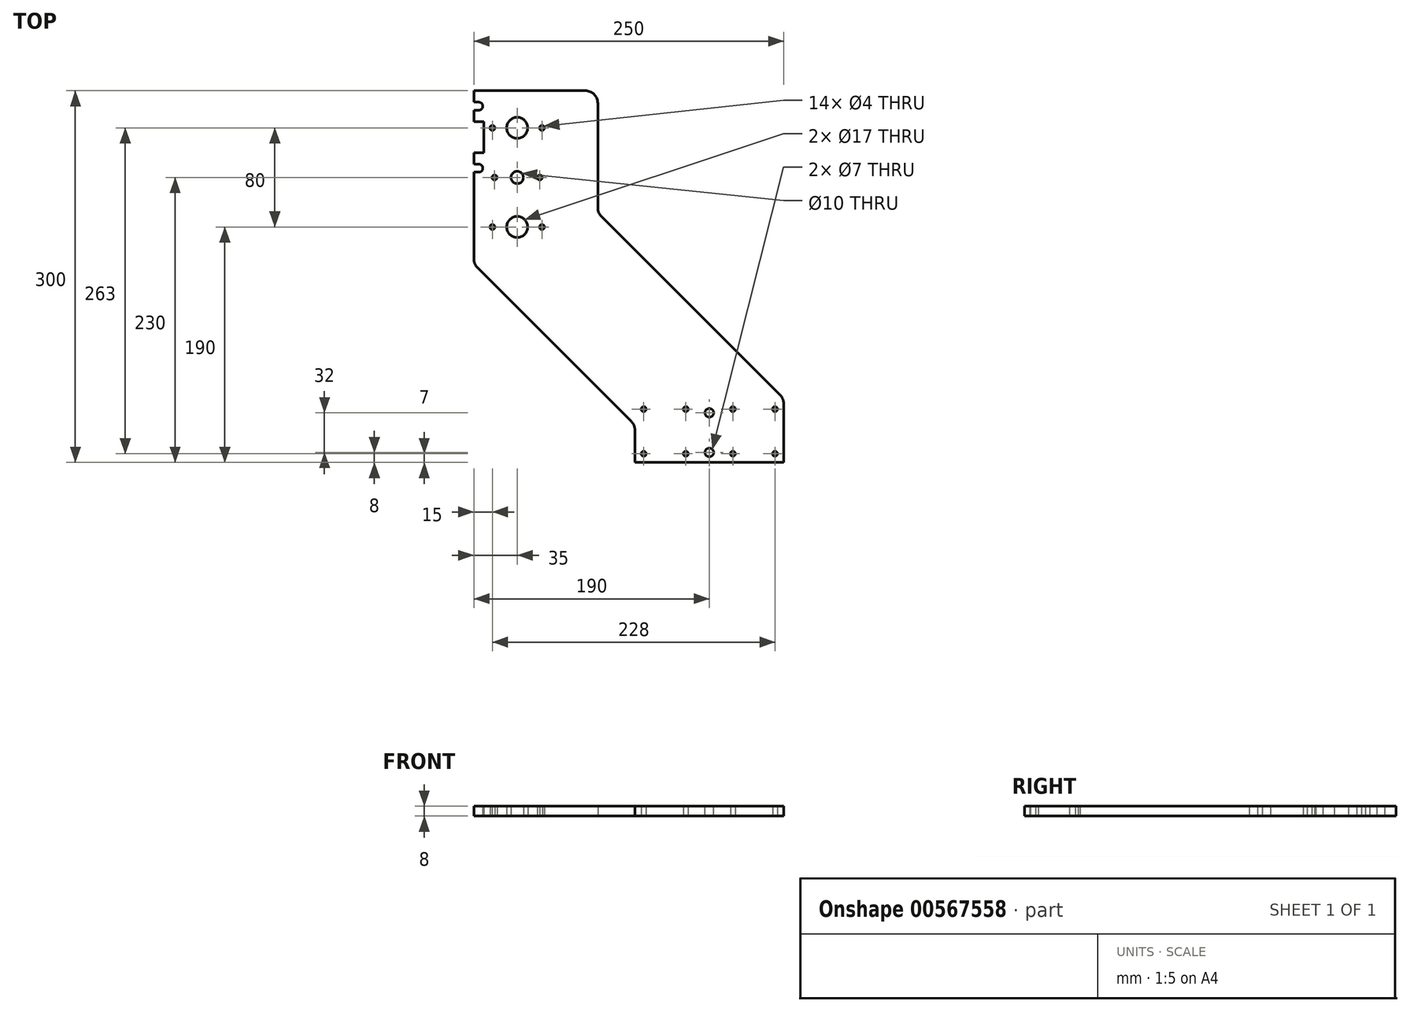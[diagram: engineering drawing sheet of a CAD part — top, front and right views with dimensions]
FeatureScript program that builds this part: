
annotation { "Feature Type Name" : "Feature", "Feature Type Description" : "" }
export const myFeature = defineFeature(function(context is Context, id is Id, definition is map)
    precondition{}
    {
        {
            var Q0;
            Q0=qCreatedBy(makeId("Top.planeOp"),FACE);
            var sketch = newSketch(context, id + "F0", { "sketchPlane" : qUnion([Q0])});
            skLineSegment(sketch, "E0", {"start": v(0, 0) * mm, "end": v(120, 0) * mm});
            skLineSegment(sketch, "E1", {"start": v(120, 0) * mm, "end": v(120, 51.42) * mm});
            skLineSegment(sketch, "E2", {"start": v(120, 51.42) * mm, "end": v(-30, 201.42) * mm});
            skLineSegment(sketch, "E3", {"start": v(-30, 201.42) * mm, "end": v(-30, 300) * mm});
            skLineSegment(sketch, "E4", {"start": v(-30, 300) * mm, "end": v(-130, 300) * mm});
            skLineSegment(sketch, "E5", {"start": v(-130, 300) * mm, "end": v(-130, 290.75) * mm});
            skLineSegment(sketch, "E6", {"start": v(-130, 160) * mm, "end": v(0, 30) * mm});
            skLineSegment(sketch, "E7", {"start": v(0, 30) * mm, "end": v(0, 0) * mm});
            skCircle(sketch, "E8", {"center": v(7, 43) * mm, "radius": 2 * mm});
            skCircle(sketch, "E9", {"center": v(7, 7) * mm, "radius": 2 * mm});
            skCircle(sketch, "E10", {"center": v(41, 43) * mm, "radius": 2 * mm});
            skCircle(sketch, "E11", {"center": v(41, 7) * mm, "radius": 2 * mm});
            skLineSegment(sketch, "E12", {"start": v(60, 0) * mm, "end": v(60, 107.18) * mm, "construction": true});
            skCircle(sketch, "E13.MirrorC", {"center": v(79, 43) * mm, "radius": 2 * mm});
            skCircle(sketch, "E14.MirrorC", {"center": v(113, 43) * mm, "radius": 2 * mm});
            skCircle(sketch, "E15.MirrorC", {"center": v(113, 7) * mm, "radius": 2 * mm});
            skCircle(sketch, "E16.MirrorC", {"center": v(79, 7) * mm, "radius": 2 * mm});
            skCircle(sketch, "E17", {"center": v(-95, 270) * mm, "radius": 8.5 * mm});
            skCircle(sketch, "E18", {"center": v(-95, 190) * mm, "radius": 8.5 * mm});
            skPoint(sketch, "E19", {"position": v(-80, 300) * mm});
            skCircle(sketch, "E20", {"center": v(-75, 270) * mm, "radius": 2 * mm});
            skCircle(sketch, "E21", {"center": v(-115, 270) * mm, "radius": 2 * mm});
            skCircle(sketch, "E22", {"center": v(-75, 190) * mm, "radius": 2 * mm});
            skCircle(sketch, "E23", {"center": v(-115, 190) * mm, "radius": 2 * mm});
            skLineSegment(sketch, "E24", {"start": v(-115, 190) * mm, "end": v(-75, 190) * mm, "construction": true});
            skLineSegment(sketch, "E25", {"start": v(-75, 270) * mm, "end": v(-115, 270) * mm, "construction": true});
            skLineSegment(sketch, "E26.bottom", {"start": v(-130, 275) * mm, "end": v(-122, 275) * mm});
            skLineSegment(sketch, "E26.top", {"start": v(-130, 250) * mm, "end": v(-122, 250) * mm});
            skLineSegment(sketch, "E26.right", {"start": v(-122, 275) * mm, "end": v(-122, 250) * mm});
            skLineSegment(sketch, "E27.trimOffspring", {"start": v(-130, 250) * mm, "end": v(-130, 160) * mm});
            skArc(sketch, "E28", {"start": v(-126, 284.25) * mm, "mid": v(-122.75, 287.5) * mm, "end": v(-126, 290.75) * mm});
            skLineSegment(sketch, "E29", {"start": v(-126, 290.75) * mm, "end": v(-130, 290.75) * mm});
            skLineSegment(sketch, "E30", {"start": v(-126, 284.25) * mm, "end": v(-130, 284.25) * mm});
            skLineSegment(sketch, "E31.trimOffspring", {"start": v(-130, 284.25) * mm, "end": v(-130, 275) * mm});
            skLineSegment(sketch, "E32", {"start": v(-89.75, 262.5) * mm, "end": v(-122, 262.5) * mm, "construction": true});
            skLineSegment(sketch, "E33.MirrorCS", {"start": v(-126, 240.75) * mm, "end": v(-130, 240.75) * mm});
            skArc(sketch, "E34.MirrorCS", {"start": v(-126, 240.75) * mm, "mid": v(-122.75, 237.5) * mm, "end": v(-126, 234.25) * mm});
            skLineSegment(sketch, "E35.MirrorCS", {"start": v(-126, 234.25) * mm, "end": v(-130, 234.25) * mm});
            skSolve(sketch);
        }
        {
            var Q0;
            Q0=makeQuery(id+"F0.imprint","IMPRINT",FACE,{"disambiguationData":[TD([[makeQuery(id+"F0.imprint","IMPRINT",EDGE,{"derivedFrom":sQuery(id+"F0.wireOp",EDGE,"E0")}),1.0]])]});
            extrude(context, id + "F1", {"entities" : qUnion([Q0]), "depth" : 8 * mm, "offsetDistance" : 25 * mm});
        }
        {
            var Q0;
            Q0=makeQuery(id+"F1.opExtrude","CAP_FACE",FACE,{"disambiguationData":[OSD([sQuery(id+"F0.wireOp",EDGE,"E0"),sQuery(id+"F0.wireOp",EDGE,"E1"),sQuery(id+"F0.wireOp",EDGE,"E2"),sQuery(id+"F0.wireOp",EDGE,"E3"),sQuery(id+"F0.wireOp",EDGE,"E4"),sQuery(id+"F0.wireOp",EDGE,"E5"),sQuery(id+"F0.wireOp",EDGE,"E6"),sQuery(id+"F0.wireOp",EDGE,"E7"),sQuery(id+"F0.wireOp",EDGE,"E8"),sQuery(id+"F0.wireOp",EDGE,"E9"),sQuery(id+"F0.wireOp",EDGE,"E10"),sQuery(id+"F0.wireOp",EDGE,"E11"),sQuery(id+"F0.wireOp",EDGE,"E13.MirrorC"),sQuery(id+"F0.wireOp",EDGE,"E14.MirrorC"),sQuery(id+"F0.wireOp",EDGE,"E15.MirrorC"),sQuery(id+"F0.wireOp",EDGE,"E16.MirrorC"),sQuery(id+"F0.wireOp",EDGE,"E17"),sQuery(id+"F0.wireOp",EDGE,"E18"),sQuery(id+"F0.wireOp",EDGE,"E20"),sQuery(id+"F0.wireOp",EDGE,"E21"),sQuery(id+"F0.wireOp",EDGE,"E22"),sQuery(id+"F0.wireOp",EDGE,"E23"),sQuery(id+"F0.wireOp",EDGE,"E26.bottom"),sQuery(id+"F0.wireOp",EDGE,"E26.top"),sQuery(id+"F0.wireOp",EDGE,"E26.right"),sQuery(id+"F0.wireOp",EDGE,"E27.trimOffspring"),sQuery(id+"F0.wireOp",EDGE,"E28"),sQuery(id+"F0.wireOp",EDGE,"E29"),sQuery(id+"F0.wireOp",EDGE,"E30"),sQuery(id+"F0.wireOp",EDGE,"E31.trimOffspring"),sQuery(id+"F0.wireOp",EDGE,"E33.MirrorCS"),sQuery(id+"F0.wireOp",EDGE,"E34.MirrorCS"),sQuery(id+"F0.wireOp",EDGE,"E35.MirrorCS")])],"isStart":false});
            var sketch = newSketch(context, id + "F2", { "sketchPlane" : qUnion([Q0])});
            skCircle(sketch, "E36", {"center": v(60, 8) * mm, "radius": 3.5 * mm});
            skCircle(sketch, "E37", {"center": v(60, 40) * mm, "radius": 3.5 * mm});
            skSolve(sketch);
        }
        {
            var Q0;
            Q0 = qSketchRegion(id + "F2", true);
            extrude(context, id + "F3", {"entities" : qUnion([Q0]), "operationType" : NewBodyOperationType.REMOVE, "endBound" : BoundingType.UP_TO_NEXT, "oppositeDirection" : true, "depth" : 25 * mm, "offsetDistance" : 25 * mm});
        }
        {
            var Q0;
            Q0=makeQuery(id+"F1.opExtrude","CAP_FACE",FACE,{"disambiguationData":[OSD([sQuery(id+"F0.wireOp",EDGE,"E0"),sQuery(id+"F0.wireOp",EDGE,"E1"),sQuery(id+"F0.wireOp",EDGE,"E2"),sQuery(id+"F0.wireOp",EDGE,"E3"),sQuery(id+"F0.wireOp",EDGE,"E4"),sQuery(id+"F0.wireOp",EDGE,"E5"),sQuery(id+"F0.wireOp",EDGE,"E6"),sQuery(id+"F0.wireOp",EDGE,"E7"),sQuery(id+"F0.wireOp",EDGE,"E8"),sQuery(id+"F0.wireOp",EDGE,"E9"),sQuery(id+"F0.wireOp",EDGE,"E10"),sQuery(id+"F0.wireOp",EDGE,"E11"),sQuery(id+"F0.wireOp",EDGE,"E13.MirrorC"),sQuery(id+"F0.wireOp",EDGE,"E14.MirrorC"),sQuery(id+"F0.wireOp",EDGE,"E15.MirrorC"),sQuery(id+"F0.wireOp",EDGE,"E16.MirrorC"),sQuery(id+"F0.wireOp",EDGE,"E17"),sQuery(id+"F0.wireOp",EDGE,"E18"),sQuery(id+"F0.wireOp",EDGE,"E20"),sQuery(id+"F0.wireOp",EDGE,"E21"),sQuery(id+"F0.wireOp",EDGE,"E22"),sQuery(id+"F0.wireOp",EDGE,"E23"),sQuery(id+"F0.wireOp",EDGE,"E26.bottom"),sQuery(id+"F0.wireOp",EDGE,"E26.top"),sQuery(id+"F0.wireOp",EDGE,"E26.right"),sQuery(id+"F0.wireOp",EDGE,"E27.trimOffspring"),sQuery(id+"F0.wireOp",EDGE,"E28"),sQuery(id+"F0.wireOp",EDGE,"E29"),sQuery(id+"F0.wireOp",EDGE,"E30"),sQuery(id+"F0.wireOp",EDGE,"E31.trimOffspring"),sQuery(id+"F0.wireOp",EDGE,"E33.MirrorCS"),sQuery(id+"F0.wireOp",EDGE,"E34.MirrorCS"),sQuery(id+"F0.wireOp",EDGE,"E35.MirrorCS")])],"isStart":true});
            var sketch = newSketch(context, id + "F4", { "sketchPlane" : qUnion([Q0])});
            skLineSegment(sketch, "E38", {"start": v(-95, -270) * mm, "end": v(-95, -190) * mm, "construction": true});
            skCircle(sketch, "E39", {"center": v(-95, -230) * mm, "radius": 5 * mm});
            skLineSegment(sketch, "E40", {"start": v(-76.75, -230) * mm, "end": v(-113.25, -230) * mm, "construction": true});
            skCircle(sketch, "E41", {"center": v(-76.75, -230) * mm, "radius": 2 * mm});
            skCircle(sketch, "E42", {"center": v(-113.25, -230) * mm, "radius": 2 * mm});
            skSolve(sketch);
        }
        {
            var Q0;
            Q0 = qSketchRegion(id + "F4", true);
            extrude(context, id + "F5", {"entities" : qUnion([Q0]), "operationType" : NewBodyOperationType.REMOVE, "endBound" : BoundingType.UP_TO_NEXT, "oppositeDirection" : true, "depth" : 25 * mm, "offsetDistance" : 25 * mm});
        }
        {
            var Q0;
            Q0=makeQuery(id+"F1.opExtrude","SWEPT_EDGE",EDGE,{"disambiguationData":[OSD([sQuery(id+"F0.wireOp",EDGE,"E6"),sQuery(id+"F0.wireOp",EDGE,"E27.trimOffspring")])]});
            var Q1;
            Q1=makeQuery(id+"F1.opExtrude","SWEPT_EDGE",EDGE,{"disambiguationData":[OSD([sQuery(id+"F0.wireOp",EDGE,"E3"),sQuery(id+"F0.wireOp",EDGE,"E4")])]});
            var Q2;
            Q2=makeQuery(id+"F1.opExtrude","SWEPT_EDGE",EDGE,{"disambiguationData":[OSD([sQuery(id+"F0.wireOp",EDGE,"E2"),sQuery(id+"F0.wireOp",EDGE,"E3")])]});
            var Q3;
            Q3=makeQuery(id+"F1.opExtrude","SWEPT_EDGE",EDGE,{"disambiguationData":[OSD([sQuery(id+"F0.wireOp",EDGE,"E1"),sQuery(id+"F0.wireOp",EDGE,"E2")])]});
            var Q4;
            Q4=makeQuery(id+"F1.opExtrude","SWEPT_EDGE",EDGE,{"disambiguationData":[OSD([sQuery(id+"F0.wireOp",EDGE,"E6"),sQuery(id+"F0.wireOp",EDGE,"E7")])]});
            fillet(context, id + "F6", {"entities" : qUnion([Q0, Q1, Q2, Q3, Q4]), "radius" : 10 * mm, "tangentPropagation" : true, "allowEdgeOverflow" : false});
        }
    });
